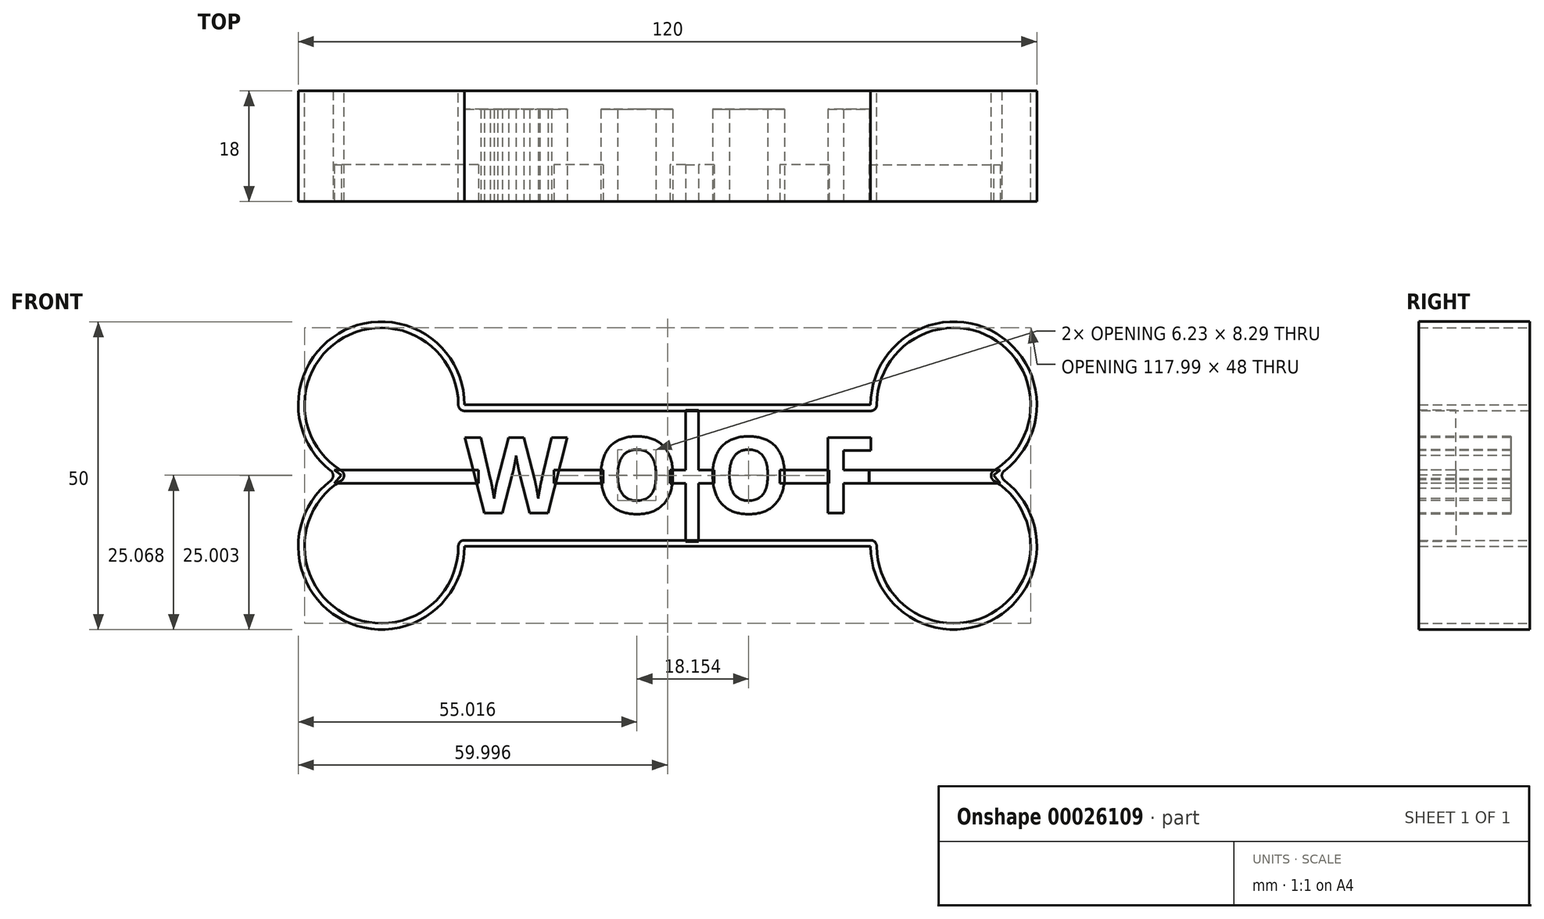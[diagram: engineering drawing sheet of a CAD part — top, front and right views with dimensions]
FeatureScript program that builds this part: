
annotation { "Feature Type Name" : "Feature", "Feature Type Description" : "" }
export const myFeature = defineFeature(function(context is Context, id is Id, definition is map)
    precondition{}
    {
        {
            var Q0;
            Q0=qCreatedBy(makeId("Front.planeOp"),FACE);
            var sketch = newSketch(context, id + "F0", { "sketchPlane" : qUnion([Q0])});
            skLineSegment(sketch, "E0.bottom", {"start": v(-19.88, 8.45) * mm, "end": v(46.12, 8.45) * mm});
            skLineSegment(sketch, "E0.top", {"start": v(-19.88, -14.55) * mm, "end": v(46.12, -14.55) * mm});
            skArc(sketch, "E1", {"start": v(-19.88, 8.45) * mm, "mid": v(-39.97, 20.24) * mm, "end": v(-40.45, -3.05) * mm});
            skArc(sketch, "E2", {"start": v(-40.45, -3.05) * mm, "mid": v(-39.97, -26.33) * mm, "end": v(-19.88, -14.55) * mm});
            skArc(sketch, "E3", {"start": v(66.69, -3.05) * mm, "mid": v(66.2, 20.24) * mm, "end": v(46.12, 8.45) * mm});
            skArc(sketch, "E4", {"start": v(46.12, -14.55) * mm, "mid": v(66.2, -26.33) * mm, "end": v(66.69, -3.05) * mm});
            skPoint(sketch, "E5", {"position": v(0, 0) * mm});
            skSolve(sketch);
        }
        {
            var Q0;
            Q0 = qSketchRegion(id + "F0", true);
            extrude(context, id + "F1", {"entities" : qUnion([Q0]), "depth" : 9 * mm});
        }
        {
            var Q0;
            Q0=makeQuery(id+"F1.opExtrude","CAP_FACE",FACE,{"disambiguationData":[OSD([sQuery(id+"F0.wireOp",EDGE,"E0.bottom"),sQuery(id+"F0.wireOp",EDGE,"E0.top"),sQuery(id+"F0.wireOp",EDGE,"E1"),sQuery(id+"F0.wireOp",EDGE,"E2"),sQuery(id+"F0.wireOp",EDGE,"E3"),sQuery(id+"F0.wireOp",EDGE,"E4")])],"isStart":false});
            var Q1;
            Q1=makeQuery(id+"F1.opExtrude","CAP_FACE",FACE,{"disambiguationData":[OSD([sQuery(id+"F0.wireOp",EDGE,"E0.bottom"),sQuery(id+"F0.wireOp",EDGE,"E0.top"),sQuery(id+"F0.wireOp",EDGE,"E1"),sQuery(id+"F0.wireOp",EDGE,"E2"),sQuery(id+"F0.wireOp",EDGE,"E3"),sQuery(id+"F0.wireOp",EDGE,"E4")])],"isStart":true});
            var Q2;
            Q2=makeQuery(id+"F1.opExtrude","SWEPT_BODY",BODY,{"disambiguationData":[OSD([sQuery(id+"F0.wireOp",EDGE,"E0.bottom"),sQuery(id+"F0.wireOp",EDGE,"E0.top"),sQuery(id+"F0.wireOp",EDGE,"E1"),sQuery(id+"F0.wireOp",EDGE,"E2"),sQuery(id+"F0.wireOp",EDGE,"E3"),sQuery(id+"F0.wireOp",EDGE,"E4")])]});
            shell(context, id + "F2", {"entities" : qUnion([Q0, Q1]), "parts" : qUnion([Q2]), "thickness" : 1 * mm});
        }
        {
            var Q0;
            Q0=makeQuery(id+"F2.opShell","OFFSET_EDGE",EDGE,{"disambiguationData":[OSD([sQuery(id+"F0.wireOp",EDGE,"E1"),sQuery(id+"F0.wireOp",EDGE,"E2")])]});
            var Q1;
            Q1=makeQuery(id+"F2.opShell","OFFSET_EDGE",EDGE,{"disambiguationData":[OSD([sQuery(id+"F0.wireOp",EDGE,"E3"),sQuery(id+"F0.wireOp",EDGE,"E4")])]});
            var Q2;
            Q2=makeQuery(id+"F2.opShell","OFFSET_EDGE",EDGE,{"disambiguationData":[OSD([sQuery(id+"F0.wireOp",EDGE,"E0.bottom"),sQuery(id+"F0.wireOp",EDGE,"E1")])]});
            var Q3;
            Q3=makeQuery(id+"F2.opShell","OFFSET_EDGE",EDGE,{"disambiguationData":[OSD([sQuery(id+"F0.wireOp",EDGE,"E0.top"),sQuery(id+"F0.wireOp",EDGE,"E2")])]});
            var Q4;
            Q4=makeQuery(id+"F2.opShell","OFFSET_EDGE",EDGE,{"disambiguationData":[OSD([sQuery(id+"F0.wireOp",EDGE,"E0.top"),sQuery(id+"F0.wireOp",EDGE,"E4")])]});
            var Q5;
            Q5=makeQuery(id+"F2.opShell","OFFSET_EDGE",EDGE,{"disambiguationData":[OSD([sQuery(id+"F0.wireOp",EDGE,"E0.bottom"),sQuery(id+"F0.wireOp",EDGE,"E3")])]});
            fillet(context, id + "F3", {"entities" : qUnion([Q0, Q1, Q2, Q3, Q4, Q5]), "radius" : 1 * mm, "tangentPropagation" : true, "allowEdgeOverflow" : false});
        }
        {
            var Q0;
            Q0=makeQuery(id+"F1.opExtrude","SWEPT_BODY",BODY,{"disambiguationData":[OSD([sQuery(id+"F0.wireOp",EDGE,"E0.bottom"),sQuery(id+"F0.wireOp",EDGE,"E0.top"),sQuery(id+"F0.wireOp",EDGE,"E1"),sQuery(id+"F0.wireOp",EDGE,"E2"),sQuery(id+"F0.wireOp",EDGE,"E3"),sQuery(id+"F0.wireOp",EDGE,"E4")])]});
            var Q1;
            Q1=qCreatedBy(makeId("Front.planeOp"),FACE);
            mirror(context, id + "F4", {"operationType" : NewBodyOperationType.ADD, "entities" : qUnion([Q0]), "mirrorPlane" : qUnion([Q1])});
        }
        {
            var Q0;
            Q0=qCreatedBy(makeId("Front.planeOp"),FACE);
            cPlane(context, id + "F5", {"entities" : qUnion([Q0]), "cplaneType" : CPlaneType.OFFSET, "offset" : 9 * mm, "width" : 150 * mm, "height" : 150 * mm});
        }
        {
            var Q0;
            Q0=qCreatedBy(id+"F5.planeOp",FACE);
            var sketch = newSketch(context, id + "F6", { "sketchPlane" : qUnion([Q0])});
            skText(sketch, "E6", { "text": "W O O F", "fontName": "OpenSans-Bold.ttf"});
            const initialGuessF6  = {"E6": [-0.0198, -0.00914, 1, 0, 0.01238]};
            skSetInitialGuess(sketch, initialGuessF6);
            skSolve(sketch);
        }
        {
            var Q0;
            Q0 = qSketchRegion(id + "F6", true);
            extrude(context, id + "F7", {"entities" : qUnion([Q0]), "oppositeDirection" : true, "depth" : 15 * mm});
        }
        {
            var Q0;
            Q0=qCreatedBy(id+"F5.planeOp",FACE);
            var sketch = newSketch(context, id + "F8", { "sketchPlane" : qUnion([Q0])});
            skLineSegment(sketch, "E7.bottom", {"start": v(45.8, -2.16) * mm, "end": v(67.19, -2.16) * mm});
            skLineSegment(sketch, "E7.top", {"start": v(45.8, -4.29) * mm, "end": v(67.19, -4.29) * mm});
            skLineSegment(sketch, "E7.left", {"start": v(45.8, -2.16) * mm, "end": v(45.8, -4.29) * mm});
            skLineSegment(sketch, "E8.bottom", {"start": v(39.34, -4.29) * mm, "end": v(31.34, -4.29) * mm});
            skLineSegment(sketch, "E8.top", {"start": v(39.34, -2.16) * mm, "end": v(31.34, -2.16) * mm});
            skLineSegment(sketch, "E8.left", {"start": v(39.34, -4.29) * mm, "end": v(39.34, -2.16) * mm});
            skLineSegment(sketch, "E8.right", {"start": v(31.34, -4.29) * mm, "end": v(31.34, -2.16) * mm});
            skLineSegment(sketch, "E9.bottom", {"start": v(20.7, -4.29) * mm, "end": v(13.5, -4.29) * mm});
            skLineSegment(sketch, "E9.top", {"start": v(20.7, -2.16) * mm, "end": v(13.5, -2.16) * mm});
            skLineSegment(sketch, "E9.left", {"start": v(20.7, -4.29) * mm, "end": v(20.7, -2.16) * mm});
            skLineSegment(sketch, "E9.right", {"start": v(13.5, -4.29) * mm, "end": v(13.5, -2.16) * mm});
            skLineSegment(sketch, "E10.bottom", {"start": v(2.63, -4.29) * mm, "end": v(-5.37, -4.29) * mm});
            skLineSegment(sketch, "E10.top", {"start": v(2.63, -2.16) * mm, "end": v(-5.37, -2.16) * mm});
            skLineSegment(sketch, "E10.left", {"start": v(2.63, -4.29) * mm, "end": v(2.63, -2.16) * mm});
            skLineSegment(sketch, "E10.right", {"start": v(-5.37, -4.29) * mm, "end": v(-5.37, -2.16) * mm});
            skLineSegment(sketch, "E11.bottom", {"start": v(-17.62, -2.16) * mm, "end": v(-41.05, -2.16) * mm});
            skLineSegment(sketch, "E11.top", {"start": v(-17.62, -4.29) * mm, "end": v(-41.05, -4.29) * mm});
            skLineSegment(sketch, "E11.left", {"start": v(-17.62, -2.16) * mm, "end": v(-17.62, -4.29) * mm});
            skLineSegment(sketch, "E12", {"start": v(67.19, -2.16) * mm, "end": v(66.1, -3) * mm});
            skLineSegment(sketch, "E13", {"start": v(66.1, -3) * mm, "end": v(67.19, -4.29) * mm});
            skLineSegment(sketch, "E14", {"start": v(-41.05, -2.16) * mm, "end": v(-39.9, -3) * mm});
            skLineSegment(sketch, "E15", {"start": v(-39.9, -3) * mm, "end": v(-41.05, -4.29) * mm});
            skLineSegment(sketch, "E16", {"start": v(17.1, -2.16) * mm, "end": v(17.1, 7.75) * mm, "construction": true});
            skLineSegment(sketch, "E17", {"start": v(17.1, 7.75) * mm, "end": v(17.1, -13.72) * mm, "construction": true});
            skLineSegment(sketch, "E18.bottom", {"start": v(16.03, -2.16) * mm, "end": v(18.16, -2.16) * mm});
            skLineSegment(sketch, "E18.top", {"start": v(16.03, 7.6) * mm, "end": v(18.16, 7.6) * mm});
            skLineSegment(sketch, "E18.left", {"start": v(16.03, -2.16) * mm, "end": v(16.03, 7.6) * mm});
            skLineSegment(sketch, "E18.right", {"start": v(18.16, -2.16) * mm, "end": v(18.16, 7.6) * mm});
            skLineSegment(sketch, "E19.bottom", {"start": v(16.03, -4.29) * mm, "end": v(18.16, -4.29) * mm});
            skLineSegment(sketch, "E19.top", {"start": v(16.03, -13.75) * mm, "end": v(18.16, -13.75) * mm});
            skLineSegment(sketch, "E19.left", {"start": v(16.03, -4.29) * mm, "end": v(16.03, -13.75) * mm});
            skLineSegment(sketch, "E19.right", {"start": v(18.16, -4.29) * mm, "end": v(18.16, -13.75) * mm});
            skSolve(sketch);
        }
        {
            var Q0;
            Q0 = qSketchRegion(id + "F8", true);
            extrude(context, id + "F9", {"entities" : qUnion([Q0]), "oppositeDirection" : true, "depth" : 6 * mm});
        }
        {
            var Q0;
            {var subQ0=makeQuery(id+"F1.opExtrude","SWEPT_EDGE",EDGE,{"disambiguationData":[OSD([sQuery(id+"F0.wireOp",EDGE,"E3"),sQuery(id+"F0.wireOp",EDGE,"E4")])]});Q0=makeQuery(id+"F4.boolean.opBoolean","MERGE",EDGE,{"derivedFrom":[subQ0,makeQuery(id+"F4.opPattern","COPY",EDGE,{"derivedFrom":subQ0,"instanceName":"1"})]});}
            var Q1;
            {var subQ0=makeQuery(id+"F1.opExtrude","SWEPT_EDGE",EDGE,{"disambiguationData":[OSD([sQuery(id+"F0.wireOp",EDGE,"E1"),sQuery(id+"F0.wireOp",EDGE,"E2")])]});Q1=makeQuery(id+"F4.boolean.opBoolean","MERGE",EDGE,{"derivedFrom":[subQ0,makeQuery(id+"F4.opPattern","COPY",EDGE,{"derivedFrom":subQ0,"instanceName":"1"})]});}
            fillet(context, id + "F10", {"entities" : qUnion([Q0, Q1]), "radius" : 1 * mm, "tangentPropagation" : true, "allowEdgeOverflow" : false});
        }
    });
